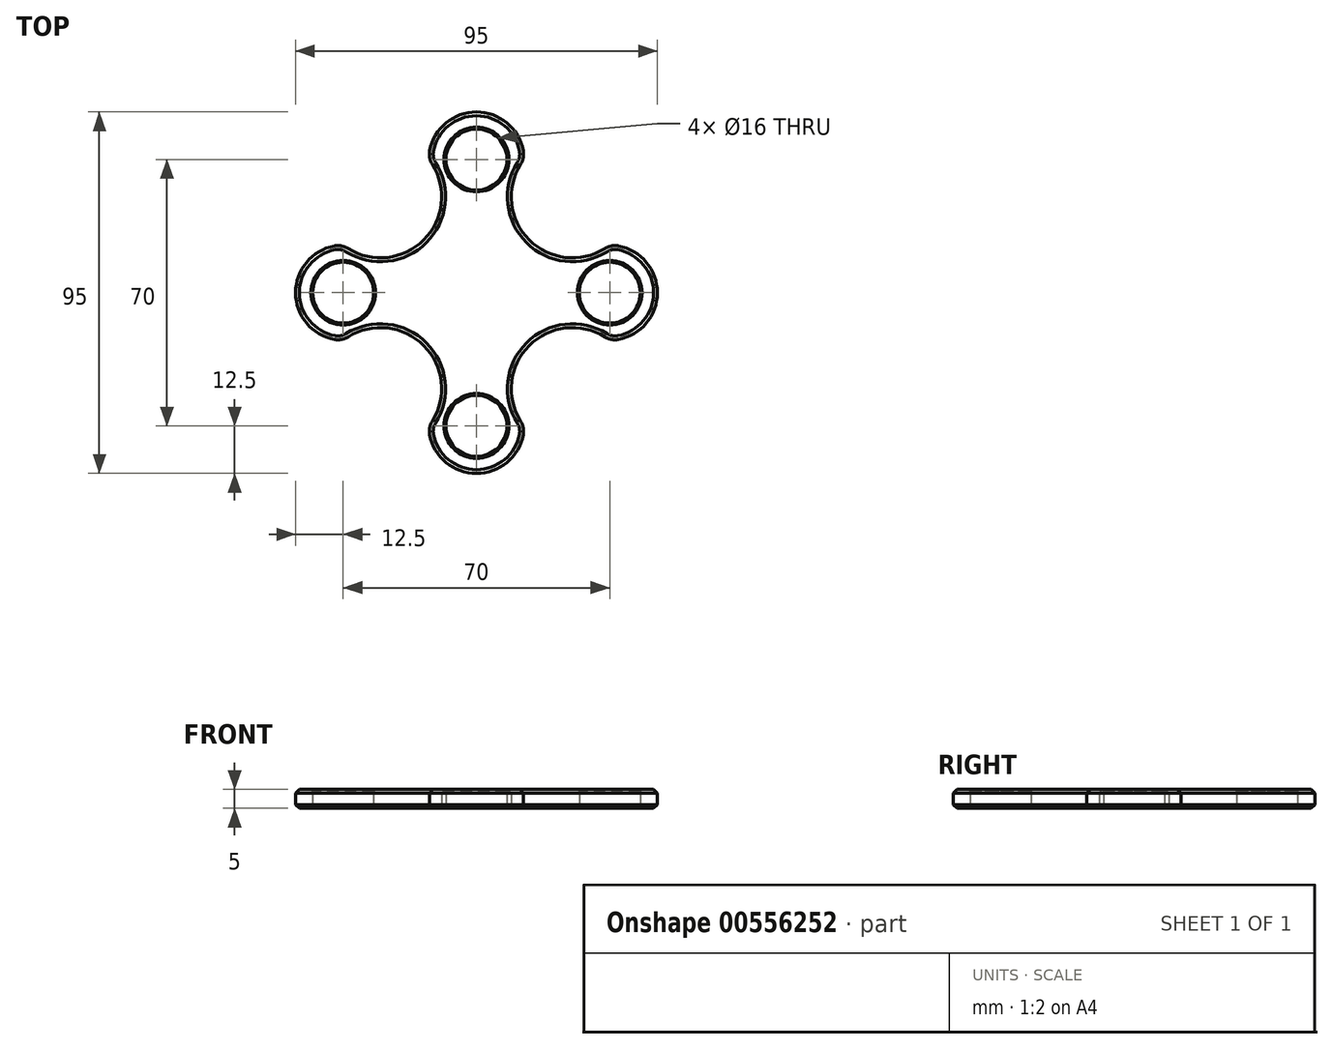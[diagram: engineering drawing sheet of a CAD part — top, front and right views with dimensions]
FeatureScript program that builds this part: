
annotation { "Feature Type Name" : "Feature", "Feature Type Description" : "" }
export const myFeature = defineFeature(function(context is Context, id is Id, definition is map)
    precondition{}
    {
        {
            var Q0;
            Q0=qCreatedBy(makeId("Top.planeOp"),FACE);
            var sketch = newSketch(context, id + "F0", { "sketchPlane" : qUnion([Q0])});
            skCircle(sketch, "E0", {"center": v(0, 35) * mm, "radius": 8 * mm});
            skArc(sketch, "E1", {"start": v(12.29, 37.3) * mm, "mid": v(0, 47.5) * mm, "end": v(-12.29, 37.3) * mm});
            skLineSegment(sketch, "E2", {"start": v(-12.5, 35) * mm, "end": v(-12.5, 22.5) * mm, "construction": true});
            skLineSegment(sketch, "E3", {"start": v(12.5, 35) * mm, "end": v(12.5, 17.5) * mm, "construction": true});
            skLineSegment(sketch, "E4.1.0", {"start": v(-35, -12.5) * mm, "end": v(-17.5, -12.5) * mm, "construction": true});
            skArc(sketch, "E4.1.1", {"start": v(-37.3, 12.29) * mm, "mid": v(-47.5, 0) * mm, "end": v(-37.3, -12.29) * mm});
            skCircle(sketch, "E4.1.2", {"center": v(-35, 0) * mm, "radius": 8 * mm});
            skLineSegment(sketch, "E4.1.3", {"start": v(-35, 12.5) * mm, "end": v(-17.5, 12.5) * mm, "construction": true});
            skLineSegment(sketch, "E5.MirrorCS", {"start": v(12.5, -35) * mm, "end": v(12.5, -17.5) * mm, "construction": true});
            skLineSegment(sketch, "E6.MirrorCS", {"start": v(-12.5, -35) * mm, "end": v(-12.5, -17.5) * mm, "construction": true});
            skArc(sketch, "E7.MirrorC", {"start": v(12.29, -37.3) * mm, "mid": v(0, -47.5) * mm, "end": v(-12.29, -37.3) * mm});
            skCircle(sketch, "E8.MirrorC", {"center": v(0, -35) * mm, "radius": 8 * mm});
            skLineSegment(sketch, "E9.MirrorCS", {"start": v(35, -12.5) * mm, "end": v(17.5, -12.5) * mm, "construction": true});
            skArc(sketch, "E10.MirrorC", {"start": v(37.3, 12.29) * mm, "mid": v(47.5, 0) * mm, "end": v(37.3, -12.29) * mm});
            skCircle(sketch, "E11.MirrorC", {"center": v(35, 0) * mm, "radius": 8 * mm});
            skLineSegment(sketch, "E12.MirrorCS", {"start": v(35, 12.5) * mm, "end": v(17.5, 12.5) * mm, "construction": true});
            skLineSegment(sketch, "E13", {"start": v(-85.05, 0) * mm, "end": v(120, 0) * mm, "construction": true});
            skLineSegment(sketch, "E14", {"start": v(0, -69) * mm, "end": v(0, 51.77) * mm, "construction": true});
            skPoint(sketch, "E15.visualSharp", {"position": v(-12.5, 12.5) * mm});
            skArc(sketch, "E16", {"start": v(-33.72, 11.6) * mm, "mid": v(-13.86, 13.86) * mm, "end": v(-11.6, 33.72) * mm});
            skArc(sketch, "E17.MirrorCS", {"start": v(33.72, 11.6) * mm, "mid": v(13.86, 13.86) * mm, "end": v(11.6, 33.72) * mm});
            skArc(sketch, "E18.MirrorCS", {"start": v(33.72, -11.6) * mm, "mid": v(13.86, -13.86) * mm, "end": v(11.6, -33.72) * mm});
            skArc(sketch, "E19.MirrorCS", {"start": v(-33.72, -11.6) * mm, "mid": v(-13.86, -13.86) * mm, "end": v(-11.6, -33.72) * mm});
            skPoint(sketch, "E20.MirrorCS.end.orphan", {"position": v(-12.5, -35) * mm});
            skPoint(sketch, "E21.MirrorCS.end.orphan", {"position": v(12.5, -35) * mm});
            skPoint(sketch, "E22.MirrorCS.end.orphan", {"position": v(12.5, 35) * mm});
            skPoint(sketch, "E23.visualSharp", {"position": v(-12.5, 35) * mm});
            skArc(sketch, "E23.filletArc", {"start": v(-12.29, 37.3) * mm, "mid": v(-12.28, 35.44) * mm, "end": v(-11.6, 33.72) * mm});
            skArc(sketch, "E24.filletArc", {"start": v(11.6, 33.72) * mm, "mid": v(12.28, 35.44) * mm, "end": v(12.29, 37.3) * mm});
            skPoint(sketch, "E25.visualSharp", {"position": v(35, 12.5) * mm});
            skArc(sketch, "E25.filletArc", {"start": v(37.3, 12.29) * mm, "mid": v(35.44, 12.28) * mm, "end": v(33.72, 11.6) * mm});
            skPoint(sketch, "E26.visualSharp", {"position": v(35, -12.5) * mm});
            skArc(sketch, "E26.filletArc", {"start": v(33.72, -11.6) * mm, "mid": v(35.44, -12.28) * mm, "end": v(37.3, -12.29) * mm});
            skArc(sketch, "E27.filletArc", {"start": v(12.29, -37.3) * mm, "mid": v(12.28, -35.44) * mm, "end": v(11.6, -33.72) * mm});
            skArc(sketch, "E28.filletArc", {"start": v(-11.6, -33.72) * mm, "mid": v(-12.28, -35.44) * mm, "end": v(-12.29, -37.3) * mm});
            skPoint(sketch, "E29.visualSharp", {"position": v(-35, -12.5) * mm});
            skArc(sketch, "E29.filletArc", {"start": v(-37.3, -12.29) * mm, "mid": v(-35.44, -12.28) * mm, "end": v(-33.72, -11.6) * mm});
            skPoint(sketch, "E30.visualSharp", {"position": v(-35, 12.5) * mm});
            skArc(sketch, "E30.filletArc", {"start": v(-33.72, 11.6) * mm, "mid": v(-35.44, 12.28) * mm, "end": v(-37.3, 12.29) * mm});
            skSolve(sketch);
        }
        {
            var Q0;
            Q0=makeQuery(id+"F0.imprint","IMPRINT",FACE,{"disambiguationData":[TD([[makeQuery(id+"F0.imprint","IMPRINT",EDGE,{"derivedFrom":sQuery(id+"F0.wireOp",EDGE,"E0")}),-1.0]])]});
            extrude(context, id + "F1", {"entities" : qUnion([Q0]), "depth" : 5 * mm, "offsetDistance" : 25 * mm});
        }
        {
            var Q0;
            Q0=makeQuery(id+"F1.opExtrude","CAP_EDGE",EDGE,{"disambiguationData":[OSD([sQuery(id+"F0.wireOp",EDGE,"E4.1.1")])],"isStart":false});
            var Q1;
            Q1=makeQuery(id+"F1.opExtrude","CAP_EDGE",EDGE,{"disambiguationData":[OSD([sQuery(id+"F0.wireOp",EDGE,"E4.1.0")])],"isStart":false});
            var Q2;
            Q2=makeQuery(id+"F1.opExtrude","CAP_EDGE",EDGE,{"disambiguationData":[OSD([sQuery(id+"F0.wireOp",EDGE,"E4.1.3")])],"isStart":false});
            var Q3;
            Q3=makeQuery(id+"F1.opExtrude","CAP_EDGE",EDGE,{"disambiguationData":[OSD([sQuery(id+"F0.wireOp",EDGE,"E2")])],"isStart":false});
            var Q4;
            Q4=makeQuery(id+"F1.opExtrude","CAP_EDGE",EDGE,{"disambiguationData":[OSD([sQuery(id+"F0.wireOp",EDGE,"E1")])],"isStart":false});
            var Q5;
            Q5=makeQuery(id+"F1.opExtrude","CAP_EDGE",EDGE,{"disambiguationData":[OSD([sQuery(id+"F0.wireOp",EDGE,"E3")])],"isStart":false});
            var Q6;
            Q6=makeQuery(id+"F1.opExtrude","CAP_EDGE",EDGE,{"disambiguationData":[OSD([sQuery(id+"F0.wireOp",EDGE,"E12.MirrorCS")])],"isStart":false});
            var Q7;
            Q7=makeQuery(id+"F1.opExtrude","CAP_EDGE",EDGE,{"disambiguationData":[OSD([sQuery(id+"F0.wireOp",EDGE,"E10.MirrorC")])],"isStart":false});
            var Q8;
            Q8=makeQuery(id+"F1.opExtrude","CAP_EDGE",EDGE,{"disambiguationData":[OSD([sQuery(id+"F0.wireOp",EDGE,"E9.MirrorCS")])],"isStart":false});
            var Q9;
            Q9=makeQuery(id+"F1.opExtrude","CAP_EDGE",EDGE,{"disambiguationData":[OSD([sQuery(id+"F0.wireOp",EDGE,"E5.MirrorCS")])],"isStart":false});
            var Q10;
            Q10=makeQuery(id+"F1.opExtrude","CAP_EDGE",EDGE,{"disambiguationData":[OSD([sQuery(id+"F0.wireOp",EDGE,"E6.MirrorCS")])],"isStart":false});
            var Q11;
            Q11=makeQuery(id+"F1.opExtrude","CAP_EDGE",EDGE,{"disambiguationData":[OSD([sQuery(id+"F0.wireOp",EDGE,"E7.MirrorC")])],"isStart":false});
            var Q12;
            Q12=makeQuery(id+"F1.opExtrude","CAP_EDGE",EDGE,{"disambiguationData":[OSD([sQuery(id+"F0.wireOp",EDGE,"E3")])],"isStart":true});
            var Q13;
            Q13=makeQuery(id+"F1.opExtrude","CAP_EDGE",EDGE,{"disambiguationData":[OSD([sQuery(id+"F0.wireOp",EDGE,"E1")])],"isStart":true});
            var Q14;
            Q14=makeQuery(id+"F1.opExtrude","CAP_EDGE",EDGE,{"disambiguationData":[OSD([sQuery(id+"F0.wireOp",EDGE,"E2")])],"isStart":true});
            var Q15;
            Q15=makeQuery(id+"F1.opExtrude","CAP_EDGE",EDGE,{"disambiguationData":[OSD([sQuery(id+"F0.wireOp",EDGE,"E4.1.3")])],"isStart":true});
            var Q16;
            Q16=makeQuery(id+"F1.opExtrude","CAP_EDGE",EDGE,{"disambiguationData":[OSD([sQuery(id+"F0.wireOp",EDGE,"E4.1.1")])],"isStart":true});
            var Q17;
            Q17=makeQuery(id+"F1.opExtrude","CAP_EDGE",EDGE,{"disambiguationData":[OSD([sQuery(id+"F0.wireOp",EDGE,"E4.1.0")])],"isStart":true});
            var Q18;
            Q18=makeQuery(id+"F1.opExtrude","CAP_EDGE",EDGE,{"disambiguationData":[OSD([sQuery(id+"F0.wireOp",EDGE,"E6.MirrorCS")])],"isStart":true});
            var Q19;
            Q19=makeQuery(id+"F1.opExtrude","CAP_EDGE",EDGE,{"disambiguationData":[OSD([sQuery(id+"F0.wireOp",EDGE,"E7.MirrorC")])],"isStart":true});
            var Q20;
            Q20=makeQuery(id+"F1.opExtrude","CAP_EDGE",EDGE,{"disambiguationData":[OSD([sQuery(id+"F0.wireOp",EDGE,"E5.MirrorCS")])],"isStart":true});
            var Q21;
            Q21=makeQuery(id+"F1.opExtrude","CAP_EDGE",EDGE,{"disambiguationData":[OSD([sQuery(id+"F0.wireOp",EDGE,"E9.MirrorCS")])],"isStart":true});
            var Q22;
            Q22=makeQuery(id+"F1.opExtrude","CAP_EDGE",EDGE,{"disambiguationData":[OSD([sQuery(id+"F0.wireOp",EDGE,"E10.MirrorC")])],"isStart":true});
            var Q23;
            Q23=makeQuery(id+"F1.opExtrude","CAP_EDGE",EDGE,{"disambiguationData":[OSD([sQuery(id+"F0.wireOp",EDGE,"E12.MirrorCS")])],"isStart":true});
            chamfer(context, id + "F2", {"entities" : qUnion([Q0, Q1, Q2, Q3, Q4, Q5, Q6, Q7, Q8, Q9, Q10, Q11, Q12, Q13, Q14, Q15, Q16, Q17, Q18, Q19, Q20, Q21, Q22, Q23]), "width" : 1 * mm, "tangentPropagation" : true});
        }
        {
            var Q0;
            Q0=makeQuery(id+"F1.opExtrude","CAP_EDGE",EDGE,{"disambiguationData":[OSD([sQuery(id+"F0.wireOp",EDGE,"E0")])],"isStart":false});
            var Q1;
            Q1=makeQuery(id+"F1.opExtrude","CAP_EDGE",EDGE,{"disambiguationData":[OSD([sQuery(id+"F0.wireOp",EDGE,"BauysmA7-PaKI-Gixg-zGTo-ScOVFYKIiByE")])],"isStart":false});
            var Q2;
            Q2=makeQuery(id+"F1.opExtrude","CAP_EDGE",EDGE,{"disambiguationData":[OSD([sQuery(id+"F0.wireOp",EDGE,"E8.MirrorC")])],"isStart":false});
            var Q3;
            Q3=makeQuery(id+"F1.opExtrude","CAP_EDGE",EDGE,{"disambiguationData":[OSD([sQuery(id+"F0.wireOp",EDGE,"E11.MirrorC")])],"isStart":false});
            var Q4;
            Q4=makeQuery(id+"F1.opExtrude","CAP_EDGE",EDGE,{"disambiguationData":[OSD([sQuery(id+"F0.wireOp",EDGE,"E4.1.2")])],"isStart":false});
            var Q5;
            Q5=makeQuery(id+"F1.opExtrude","CAP_EDGE",EDGE,{"disambiguationData":[OSD([sQuery(id+"F0.wireOp",EDGE,"E0")])],"isStart":true});
            var Q6;
            Q6=makeQuery(id+"F1.opExtrude","CAP_EDGE",EDGE,{"disambiguationData":[OSD([sQuery(id+"F0.wireOp",EDGE,"E4.1.2")])],"isStart":true});
            var Q7;
            Q7=makeQuery(id+"F1.opExtrude","CAP_EDGE",EDGE,{"disambiguationData":[OSD([sQuery(id+"F0.wireOp",EDGE,"BauysmA7-PaKI-Gixg-zGTo-ScOVFYKIiByE")])],"isStart":true});
            var Q8;
            Q8=makeQuery(id+"F1.opExtrude","CAP_EDGE",EDGE,{"disambiguationData":[OSD([sQuery(id+"F0.wireOp",EDGE,"E11.MirrorC")])],"isStart":true});
            var Q9;
            Q9=makeQuery(id+"F1.opExtrude","CAP_EDGE",EDGE,{"disambiguationData":[OSD([sQuery(id+"F0.wireOp",EDGE,"E8.MirrorC")])],"isStart":true});
            chamfer(context, id + "F3", {"entities" : qUnion([Q0, Q1, Q2, Q3, Q4, Q5, Q6, Q7, Q8, Q9]), "width" : .5 * mm, "tangentPropagation" : true});
        }
    });
